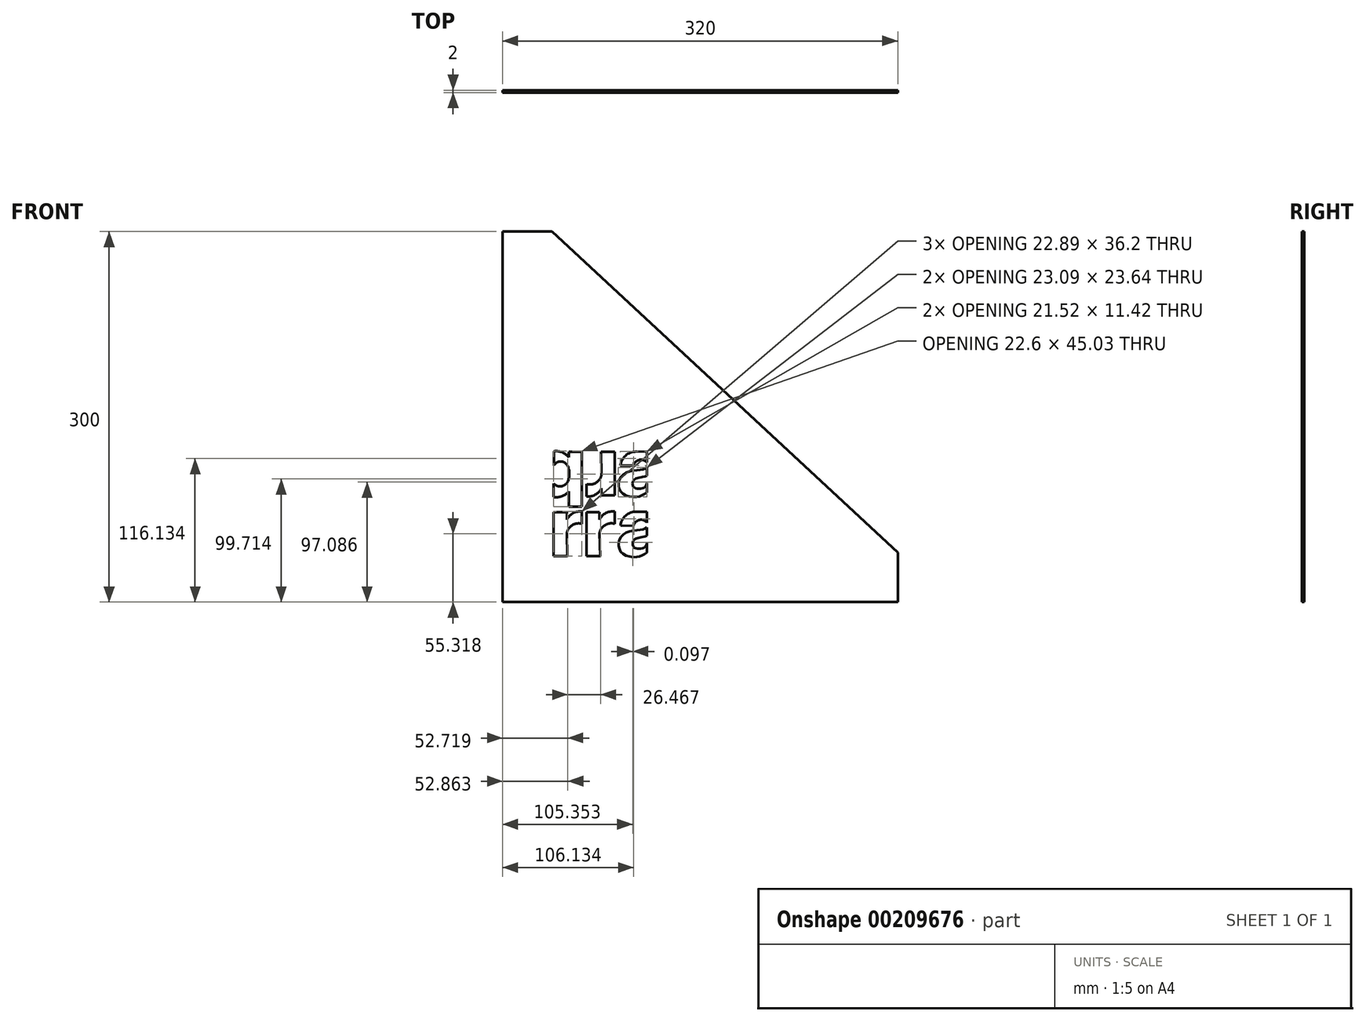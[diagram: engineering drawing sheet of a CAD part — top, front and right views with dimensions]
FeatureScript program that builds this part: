
annotation { "Feature Type Name" : "Feature", "Feature Type Description" : "" }
export const myFeature = defineFeature(function(context is Context, id is Id, definition is map)
    precondition{}
    {
        {
            var Q0;
            Q0=qCreatedBy(makeId("Front.planeOp"),FACE);
            var sketch = newSketch(context, id + "F0", { "sketchPlane" : qUnion([Q0])});
            skLineSegment(sketch, "E0.left", {"start": v(207.86, 32.3) * mm, "end": v(207.86, 332.3) * mm});
            skLineSegment(sketch, "E1", {"start": v(207.86, 333) * mm, "end": v(207.86, 33) * mm});
            skLineSegment(sketch, "E2.MirrorCS", {"start": v(249.28, 118.03) * mm, "end": v(249.28, 129.03) * mm});
            skLineSegment(sketch, "E3.MirrorCS", {"start": v(527.86, 33) * mm, "end": v(527.86, 73) * mm});
            skLineSegment(sketch, "E4.MirrorCS", {"start": v(527.86, 33) * mm, "end": v(207.86, 33) * mm});
            skLineSegment(sketch, "E5.MirrorCS", {"start": v(207.86, 333) * mm, "end": v(247.86, 333) * mm});
            skLineSegment(sketch, "E6.MirrorCS", {"start": v(247.86, 333) * mm, "end": v(527.86, 73) * mm});
            skPoint(sketch, "E7.MirrorP", {"position": v(247.86, 333) * mm});
            skPoint(sketch, "E8.MirrorP", {"position": v(527.86, 73) * mm});
            skLineSegment(sketch, "E9.MirrorCS", {"start": v(207.86, 33) * mm, "end": v(527.86, 33) * mm});
            skLineSegment(sketch, "E10.MirrorCS", {"start": v(249.28, 70.22) * mm, "end": v(249.28, 105.62) * mm});
            skPoint(sketch, "E11.MirrorP", {"position": v(527.86, 333) * mm});
            skLineSegment(sketch, "E12.MirrorCS", {"start": v(324.85, 72.99) * mm, "end": v(324.85, 80.66) * mm});
            skLineSegment(sketch, "E13.MirrorCS", {"start": v(324.85, 93.28) * mm, "end": v(324.85, 86.62) * mm});
            skLineSegment(sketch, "E14.MirrorCS", {"start": v(324.76, 141.9) * mm, "end": v(324.76, 135.24) * mm});
            skLineSegment(sketch, "E15.MirrorCS", {"start": v(324.76, 121.61) * mm, "end": v(324.76, 129.28) * mm});
            skLineSegment(sketch, "E16.MirrorCS", {"start": v(271.88, 110.2) * mm, "end": v(261.57, 110.2) * mm});
            skArc(sketch, "E17.MirrorCS", {"start": v(260.42, 143.61) * mm, "mid": v(254.87, 146.84) * mm, "end": v(249.33, 143.61) * mm});
            skArc(sketch, "E18.MirrorCS", {"start": v(324.76, 145.97) * mm, "mid": v(318.52, 148.08) * mm, "end": v(313.86, 143.42) * mm});
            skLineSegment(sketch, "E19.MirrorCS", {"start": v(324.85, 106.19) * mm, "end": v(324.85, 97.35) * mm});
            skLineSegment(sketch, "E20.MirrorCS", {"start": v(259.9, 105.62) * mm, "end": v(259.9, 99.71) * mm});
            skArc(sketch, "E21.MirrorCS", {"start": v(324.85, 97.35) * mm, "mid": v(318.61, 99.46) * mm, "end": v(313.96, 94.8) * mm});
            skArc(sketch, "E22.MirrorCS", {"start": v(272.17, 106.32) * mm, "mid": v(264.97, 105) * mm, "end": v(259.9, 99.71) * mm});
            skArc(sketch, "E23.MirrorCS", {"start": v(272.17, 96.32) * mm, "mid": v(264.43, 95.36) * mm, "end": v(259.94, 88.98) * mm});
            skLineSegment(sketch, "E24.MirrorCS", {"start": v(288, 119.28) * mm, "end": v(288, 125.19) * mm});
            skArc(sketch, "E25.MirrorCS", {"start": v(260.42, 130.1) * mm, "mid": v(261.93, 136.86) * mm, "end": v(260.42, 143.61) * mm});
            skArc(sketch, "E26.MirrorCS", {"start": v(275.75, 128.58) * mm, "mid": v(283.49, 129.54) * mm, "end": v(287.97, 135.92) * mm});
            skLineSegment(sketch, "E27.MirrorCS", {"start": v(261.57, 150.08) * mm, "end": v(261.57, 154.68) * mm});
            skArc(sketch, "E28.MirrorCS", {"start": v(298.65, 106.34) * mm, "mid": v(291.45, 105.01) * mm, "end": v(286.4, 99.73) * mm});
            skLineSegment(sketch, "E29.MirrorCS", {"start": v(316, 154.85) * mm, "end": v(324.76, 154.8) * mm});
            skArc(sketch, "E30.MirrorCS", {"start": v(261.57, 150.08) * mm, "mid": v(256.22, 154.22) * mm, "end": v(249.5, 155.12) * mm});
            skLineSegment(sketch, "E31.MirrorCS", {"start": v(324.76, 154.8) * mm, "end": v(324.76, 145.97) * mm});
            skLineSegment(sketch, "E32.MirrorCS", {"start": v(272.17, 106.32) * mm, "end": v(272.17, 96.32) * mm});
            skArc(sketch, "E33.MirrorCS", {"start": v(275.75, 118.58) * mm, "mid": v(282.94, 119.9) * mm, "end": v(288, 125.19) * mm});
            skLineSegment(sketch, "E34.MirrorCS", {"start": v(316.1, 106.22) * mm, "end": v(324.85, 106.19) * mm});
            skArc(sketch, "E35.MirrorCS", {"start": v(298.65, 96.34) * mm, "mid": v(290.91, 95.37) * mm, "end": v(286.43, 89) * mm});
            skLineSegment(sketch, "E36.MirrorCS", {"start": v(313.96, 94.8) * mm, "end": v(303.33, 94.9) * mm});
            skLineSegment(sketch, "E37.MirrorCS", {"start": v(275.76, 105.64) * mm, "end": v(286.4, 105.64) * mm});
            skLineSegment(sketch, "E38.MirrorCS", {"start": v(287.56, 154.68) * mm, "end": v(298.63, 154.68) * mm});
            skLineSegment(sketch, "E39.MirrorCS", {"start": v(313.86, 143.42) * mm, "end": v(303.23, 143.53) * mm});
            skArc(sketch, "E40.MirrorCS", {"start": v(249.28, 129.03) * mm, "mid": v(255.13, 126.67) * mm, "end": v(260.42, 130.1) * mm});
            skLineSegment(sketch, "E41.MirrorCS", {"start": v(275.75, 118.58) * mm, "end": v(275.75, 128.58) * mm});
            skLineSegment(sketch, "E42.MirrorCS", {"start": v(286.84, 70.23) * mm, "end": v(275.76, 70.23) * mm});
            skLineSegment(sketch, "E43.MirrorCS", {"start": v(298.65, 106.34) * mm, "end": v(298.65, 96.34) * mm});
            skLineSegment(sketch, "E44.MirrorCS", {"start": v(249.28, 105.62) * mm, "end": v(259.9, 105.62) * mm});
            skFitSpline(sketch, "E45.MirrorCS", {"points": [v(324.76, 129.28) * mm, v(322.83, 125.95) * mm, v(317.92, 124.78) * mm, v(313.77, 126.34) * mm, v(313.62, 131.06) * mm, v(317.64, 133.54) * mm, v(324.76, 135.24) * mm], "startDerivative": vector(-9.57, -26.3) * mm, "endDerivative": vector(42.8, 14.9) * mm});
            skLineSegment(sketch, "E46.MirrorCS", {"start": v(249.5, 155.12) * mm, "end": v(249.33, 143.61) * mm});
            skLineSegment(sketch, "E47.MirrorCS", {"start": v(261.57, 154.68) * mm, "end": v(271.88, 154.68) * mm});
            skLineSegment(sketch, "E48.MirrorCS", {"start": v(286.4, 105.64) * mm, "end": v(286.4, 99.73) * mm});
            skLineSegment(sketch, "E49.MirrorCS", {"start": v(298.63, 119.28) * mm, "end": v(288, 119.28) * mm});
            skLineSegment(sketch, "E50.MirrorCS", {"start": v(261.57, 110.2) * mm, "end": v(261.57, 122.63) * mm});
            skFitSpline(sketch, "E51.MirrorCS", {"points": [v(324.85, 80.66) * mm, v(322.93, 77.33) * mm, v(318.02, 76.16) * mm, v(313.87, 77.71) * mm, v(313.71, 82.44) * mm, v(317.74, 84.92) * mm, v(324.85, 86.62) * mm], "startDerivative": vector(-9.57, -26.3) * mm, "endDerivative": vector(42.8, 14.9) * mm});
            skLineSegment(sketch, "E52.MirrorCS", {"start": v(260.35, 70.22) * mm, "end": v(249.28, 70.22) * mm});
            skArc(sketch, "E53.MirrorCS", {"start": v(249.28, 118.03) * mm, "mid": v(256, 118.77) * mm, "end": v(261.57, 122.63) * mm});
            skFitSpline(sketch, "E54.MirrorCS", {"points": [v(324.76, 141.9) * mm, v(319.42, 140.2) * mm, v(306.8, 137.18) * mm, v(301.69, 128.82) * mm, v(305.64, 120.37) * mm, v(317.64, 118.28) * mm, v(324.76, 121.61) * mm], "startDerivative": vector(-36.18, -29.19) * mm, "endDerivative": vector(54.96, 28.77) * mm});
            skLineSegment(sketch, "E55.MirrorCS", {"start": v(298.63, 154.68) * mm, "end": v(298.63, 119.28) * mm});
            skFitSpline(sketch, "E56.MirrorCS", {"points": [v(324.85, 93.28) * mm, v(319.52, 91.58) * mm, v(306.9, 88.56) * mm, v(301.78, 80.2) * mm, v(305.73, 71.75) * mm, v(317.74, 69.66) * mm, v(324.85, 72.99) * mm], "startDerivative": vector(-36.18, -29.19) * mm, "endDerivative": vector(54.96, 28.77) * mm});
            skArc(sketch, "E57.MirrorCS", {"start": v(316, 154.85) * mm, "mid": v(307.45, 151.63) * mm, "end": v(303.23, 143.53) * mm});
            skLineSegment(sketch, "E58.MirrorCS", {"start": v(260.35, 70.22) * mm, "end": v(259.94, 88.98) * mm});
            skLineSegment(sketch, "E59.MirrorCS", {"start": v(286.84, 70.23) * mm, "end": v(286.43, 89) * mm});
            skLineSegment(sketch, "E60.MirrorCS", {"start": v(287.56, 154.68) * mm, "end": v(287.97, 135.92) * mm});
            skLineSegment(sketch, "E61.MirrorCS", {"start": v(271.88, 154.68) * mm, "end": v(271.88, 110.2) * mm});
            skLineSegment(sketch, "E62.MirrorCS", {"start": v(275.76, 70.23) * mm, "end": v(275.76, 105.64) * mm});
            skArc(sketch, "E63.MirrorCS", {"start": v(316.1, 106.22) * mm, "mid": v(307.55, 103) * mm, "end": v(303.33, 94.9) * mm});
            skSolve(sketch);
        }
        {
            var Q0;
            Q0=qSketchRegion(id+"F0",true);
            extrude(context, id + "F1", {"entities" : qUnion([Q0]), "depth" : 2 * mm});
        }
    });
